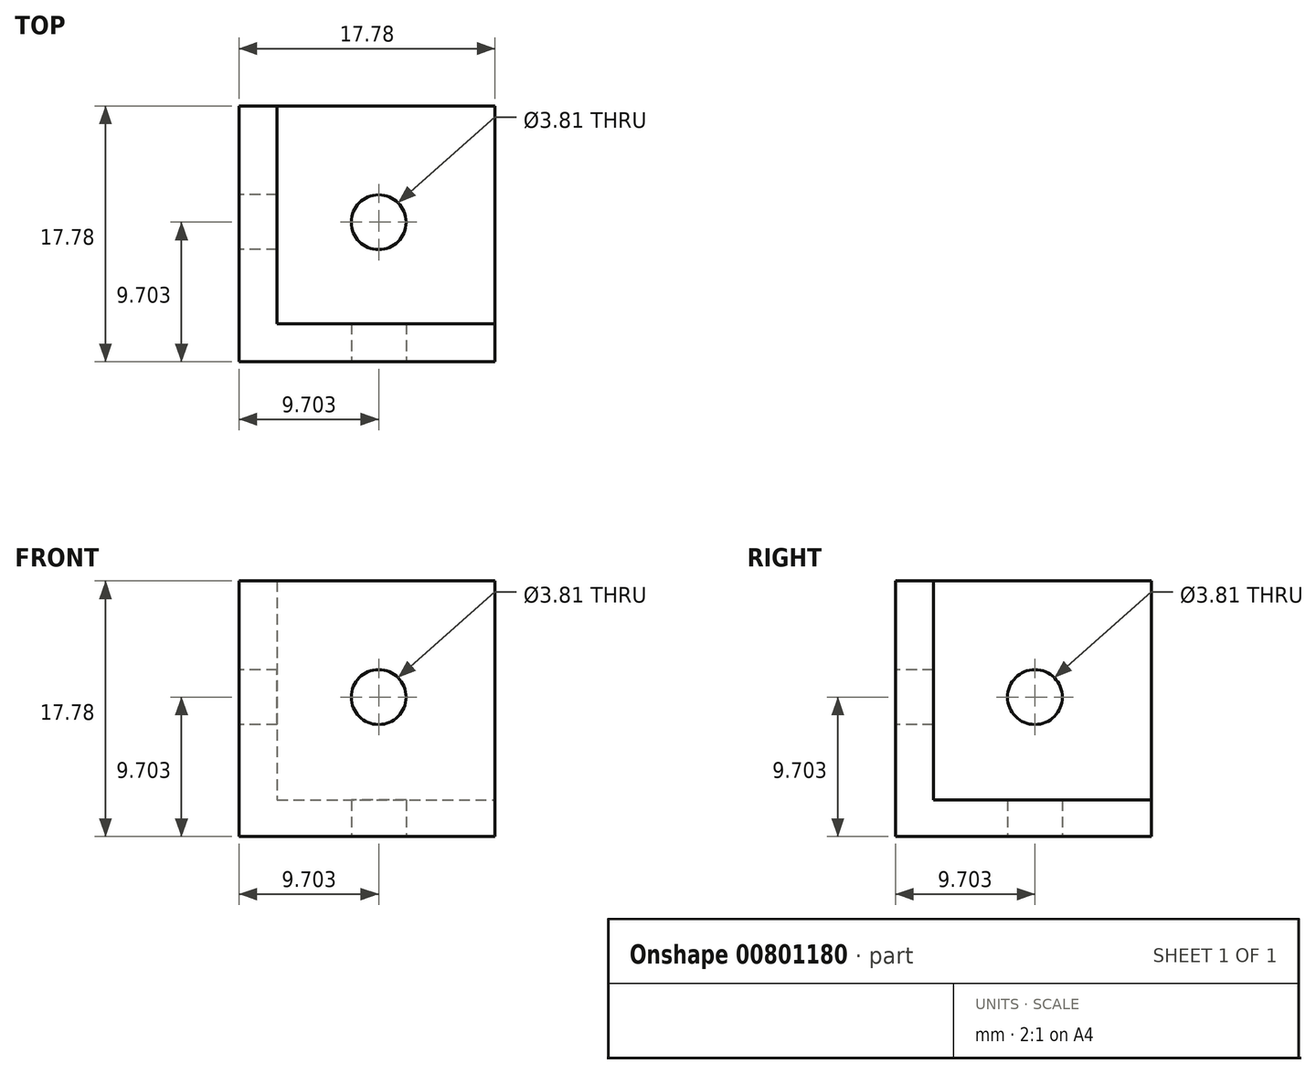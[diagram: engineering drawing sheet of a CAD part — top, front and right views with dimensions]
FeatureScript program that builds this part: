
annotation { "Feature Type Name" : "Feature", "Feature Type Description" : "" }
export const myFeature = defineFeature(function(context is Context, id is Id, definition is map)
    precondition{}
    {
        {
            var Q0;
            Q0=qCreatedBy(makeId("Top.planeOp"),FACE);
            var sketch = newSketch(context, id + "F0", { "sketchPlane" : qUnion([Q0])});
            skLineSegment(sketch, "E0.bottom", {"start": v(0, 0) * mm, "end": v(17.78, 0) * mm});
            skLineSegment(sketch, "E0.top", {"start": v(0, 17.78) * mm, "end": v(17.78, 17.78) * mm});
            skLineSegment(sketch, "E0.left", {"start": v(0, 0) * mm, "end": v(0, 17.78) * mm});
            skLineSegment(sketch, "E0.right", {"start": v(17.78, 0) * mm, "end": v(17.78, 17.78) * mm});
            skCircle(sketch, "E1", {"center": v(9.7, 9.7) * mm, "radius": 1.9 * mm});
            skSolve(sketch);
        }
        {
            var Q0;
            Q0=makeQuery(id+"F0.imprint","IMPRINT",FACE,{"disambiguationData":[TD([[makeQuery(id+"F0.imprint","IMPRINT",EDGE,{"derivedFrom":sQuery(id+"F0.wireOp",EDGE,"E0.bottom")}),1.0]])]});
            extrude(context, id + "F1", {"entities" : qUnion([Q0]), "depth" : 2.54 * mm, "offsetDistance" : 25.4 * mm});
        }
        {
            var Q0;
            Q0=makeQuery(id+"F1.opExtrude","CAP_FACE",FACE,{"disambiguationData":[OSD([sQuery(id+"F0.wireOp",EDGE,"E0.bottom"),sQuery(id+"F0.wireOp",EDGE,"E0.top"),sQuery(id+"F0.wireOp",EDGE,"E0.left"),sQuery(id+"F0.wireOp",EDGE,"E0.right"),sQuery(id+"F0.wireOp",EDGE,"E1")])],"isStart":false});
            var sketch = newSketch(context, id + "F2", { "sketchPlane" : qUnion([Q0])});
            skLineSegment(sketch, "E2", {"start": v(0, 17.78) * mm, "end": v(2.64, 17.78) * mm});
            skLineSegment(sketch, "E3", {"start": v(2.64, 17.78) * mm, "end": v(2.64, 2.64) * mm});
            skLineSegment(sketch, "E4", {"start": v(2.64, 2.64) * mm, "end": v(17.78, 2.64) * mm});
            skLineSegment(sketch, "E5", {"start": v(17.78, 2.64) * mm, "end": v(17.78, 0) * mm});
            skLineSegment(sketch, "E6", {"start": v(17.78, 0) * mm, "end": v(0, 0) * mm});
            skLineSegment(sketch, "E7", {"start": v(0, 0) * mm, "end": v(0, 17.78) * mm});
            skSolve(sketch);
        }
        {
            var Q0;
            Q0=makeQuery(id+"F2.imprint","IMPRINT",FACE,{"disambiguationData":[TD([[makeQuery(id+"F2.imprint","IMPRINT",EDGE,{"derivedFrom":sQuery(id+"F2.wireOp",EDGE,"E2")}),-1.0]])]});
            extrude(context, id + "F3", {"entities" : qUnion([Q0]), "operationType" : NewBodyOperationType.ADD, "depth" : 12.7 * mm, "offsetDistance" : 25.4 * mm});
        }
        {
            var Q0;
            Q0=makeQuery(id+"F3.boolean.opBoolean","MERGE",FACE,{"derivedFrom":[makeQuery(id+"F1.opExtrude","SWEPT_FACE",FACE,{"disambiguationData":[OSD([sQuery(id+"F0.wireOp",EDGE,"E0.bottom")])]}),makeQuery(id+"F3.opExtrude","SWEPT_FACE",FACE,{"disambiguationData":[OSD([sQuery(id+"F2.wireOp",EDGE,"E6")])]})]});
            var sketch = newSketch(context, id + "F4", { "sketchPlane" : qUnion([Q0])});
            skCircle(sketch, "E8", {"center": v(9.7, 9.7) * mm, "radius": 1.9 * mm});
            skSolve(sketch);
        }
        {
            var Q0;
            Q0=makeQuery(id+"F4.imprint","IMPRINT",FACE,{"disambiguationData":[TD([[makeQuery(id+"F4.imprint","IMPRINT",EDGE,{"derivedFrom":sQuery(id+"F4.wireOp",EDGE,"E8")}),1.0]])]});
            extrude(context, id + "F5", {"entities" : qUnion([Q0]), "operationType" : NewBodyOperationType.REMOVE, "oppositeDirection" : true, "depth" : 25.4 * mm, "offsetDistance" : 25.4 * mm});
        }
        {
            var Q0;
            Q0=makeQuery(id+"F3.boolean.opBoolean","MERGE",FACE,{"derivedFrom":[makeQuery(id+"F1.opExtrude","SWEPT_FACE",FACE,{"disambiguationData":[OSD([sQuery(id+"F0.wireOp",EDGE,"E0.left")])]}),makeQuery(id+"F3.opExtrude","SWEPT_FACE",FACE,{"disambiguationData":[OSD([sQuery(id+"F2.wireOp",EDGE,"E7")])]})]});
            var sketch = newSketch(context, id + "F6", { "sketchPlane" : qUnion([Q0])});
            skCircle(sketch, "E9", {"center": v(-9.7, 9.7) * mm, "radius": 1.9 * mm});
            skSolve(sketch);
        }
        {
            var Q0;
            Q0=makeQuery(id+"F6.imprint","IMPRINT",FACE,{"disambiguationData":[TD([[makeQuery(id+"F6.imprint","IMPRINT",EDGE,{"derivedFrom":sQuery(id+"F6.wireOp",EDGE,"E9")}),1.0]])]});
            extrude(context, id + "F7", {"entities" : qUnion([Q0]), "operationType" : NewBodyOperationType.REMOVE, "oppositeDirection" : true, "depth" : 25.4 * mm, "offsetDistance" : 25.4 * mm});
        }
        {
            var Q0;
            Q0=makeQuery(id+"F3.opExtrude","CAP_FACE",FACE,{"disambiguationData":[OSD([sQuery(id+"F2.wireOp",EDGE,"E2"),sQuery(id+"F2.wireOp",EDGE,"E3"),sQuery(id+"F2.wireOp",EDGE,"E4"),sQuery(id+"F2.wireOp",EDGE,"E5"),sQuery(id+"F2.wireOp",EDGE,"E6"),sQuery(id+"F2.wireOp",EDGE,"E7")])],"isStart":false});
            extrude(context, id + "F8", {"entities" : qUnion([Q0]), "operationType" : NewBodyOperationType.ADD, "depth" : 2.54 * mm, "offsetDistance" : 25.4 * mm});
        }
    });
